# Revit family: P1280_End_Cap
name_source: partatom
category: Generic Models
units: mm (PartAtom-declared; Revit-internal decimal feet)

## family parameters
Always vertical = No
Can host rebar = No
Cut with Voids When Loaded = No
Part Type = Normal
Room Calculation Point = No
Round Connector Dimension = Use Diameter
Shared = No
Work Plane-Based = Yes

## types (7) — shared parameters
Cost = $0.00
Description = P1280 - End Cap
Manufacturer = Atkore Unistrut
Model = P1280
Salsify ID1 = US-P1280
URL = https://www.atkore.com
Weight = 0.11 lb
zero-valued in all types: Default Elevation

## per-type parameters (varying)
| type | Material | UPC |
| P1280 DF | Defender | "786364052465" |
| P1280 EG | Electro Galvanized | "786364128009" |
| P1280 GR | Green | "0" |
| P1280 HG | Hot Dip Galvanized | "786364019482" |
| P1280 PL | Plain | "786364891248" |
| P1280 SS | Stainless Steel | "786364019499" |
| P1280 ZD | Zinc Dichromate | "786364025957" |

note: column(s) folded — value = type name in every type: Part Number

## geometry (parser evidence)
native form markers: Sweep x2
no freeform markers — native parametric forms only
